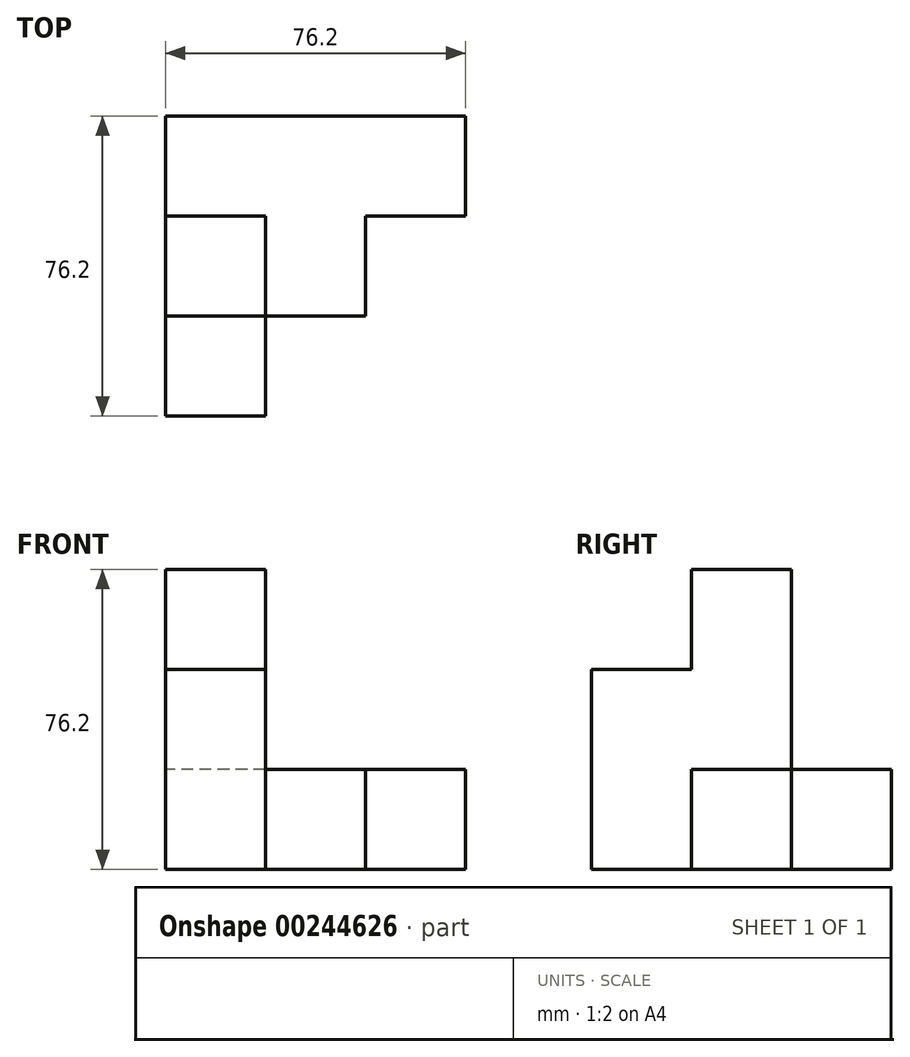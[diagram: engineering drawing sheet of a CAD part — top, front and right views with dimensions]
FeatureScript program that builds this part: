
annotation { "Feature Type Name" : "Feature", "Feature Type Description" : "" }
export const myFeature = defineFeature(function(context is Context, id is Id, definition is map)
    precondition{}
    {
        {
            var Q0;
            Q0=qCreatedBy(makeId("Top.planeOp"),FACE);
            var sketch = newSketch(context, id + "F0", { "sketchPlane" : qUnion([Q0])});
            skLineSegment(sketch, "E0.bottom", {"start": v(0, 0) * mm, "end": v(-25.4, 0) * mm});
            skLineSegment(sketch, "E0.top", {"start": v(0, 25.4) * mm, "end": v(-25.4, 25.4) * mm});
            skLineSegment(sketch, "E0.left", {"start": v(0, 0) * mm, "end": v(0, 25.4) * mm});
            skLineSegment(sketch, "E0.right", {"start": v(-25.4, 0) * mm, "end": v(-25.4, 25.4) * mm});
            skLineSegment(sketch, "E1", {"start": v(-25.4, 25.4) * mm, "end": v(-25.4, 50.8) * mm});
            skLineSegment(sketch, "E2", {"start": v(-25.4, 50.8) * mm, "end": v(50.8, 50.8) * mm});
            skLineSegment(sketch, "E3", {"start": v(50.8, 50.8) * mm, "end": v(50.8, 25.4) * mm});
            skLineSegment(sketch, "E4", {"start": v(50.8, 25.4) * mm, "end": v(25.4, 25.4) * mm});
            skLineSegment(sketch, "E5", {"start": v(25.4, 25.4) * mm, "end": v(25.4, 0) * mm});
            skLineSegment(sketch, "E6", {"start": v(25.4, 0) * mm, "end": v(0, 0) * mm});
            skLineSegment(sketch, "E7", {"start": v(-25.4, 0) * mm, "end": v(-25.4, -25.4) * mm});
            skLineSegment(sketch, "E8", {"start": v(-25.4, -25.4) * mm, "end": v(0, -25.4) * mm});
            skLineSegment(sketch, "E9", {"start": v(0, -25.4) * mm, "end": v(0, 0) * mm});
            skSolve(sketch);
        }
        {
            var Q0;
            Q0=makeQuery(id+"F0.imprint","IMPRINT",FACE,{"disambiguationData":[TD([[makeQuery(id+"F0.imprint","IMPRINT",EDGE,{"derivedFrom":sQuery(id+"F0.wireOp",EDGE,"E0.top")}),-1.0]])]});
            extrude(context, id + "F1", {"entities" : qUnion([Q0]), "depth" : 25.4 * mm});
        }
        {
            var Q0;
            Q0=makeQuery(id+"F0.imprint","IMPRINT",FACE,{"disambiguationData":[TD([[makeQuery(id+"F0.imprint","IMPRINT",EDGE,{"derivedFrom":sQuery(id+"F0.wireOp",EDGE,"E0.bottom")}),-1.0]])]});
            extrude(context, id + "F2", {"entities" : qUnion([Q0]), "operationType" : NewBodyOperationType.ADD, "depth" : 76.2 * mm});
        }
        {
            var Q0;
            Q0=makeQuery(id+"F0.imprint","IMPRINT",FACE,{"disambiguationData":[TD([[makeQuery(id+"F0.imprint","IMPRINT",EDGE,{"derivedFrom":sQuery(id+"F0.wireOp",EDGE,"E0.bottom")}),1.0]])]});
            extrude(context, id + "F3", {"entities" : qUnion([Q0]), "operationType" : NewBodyOperationType.ADD, "depth" : 50.8 * mm});
        }
    });
